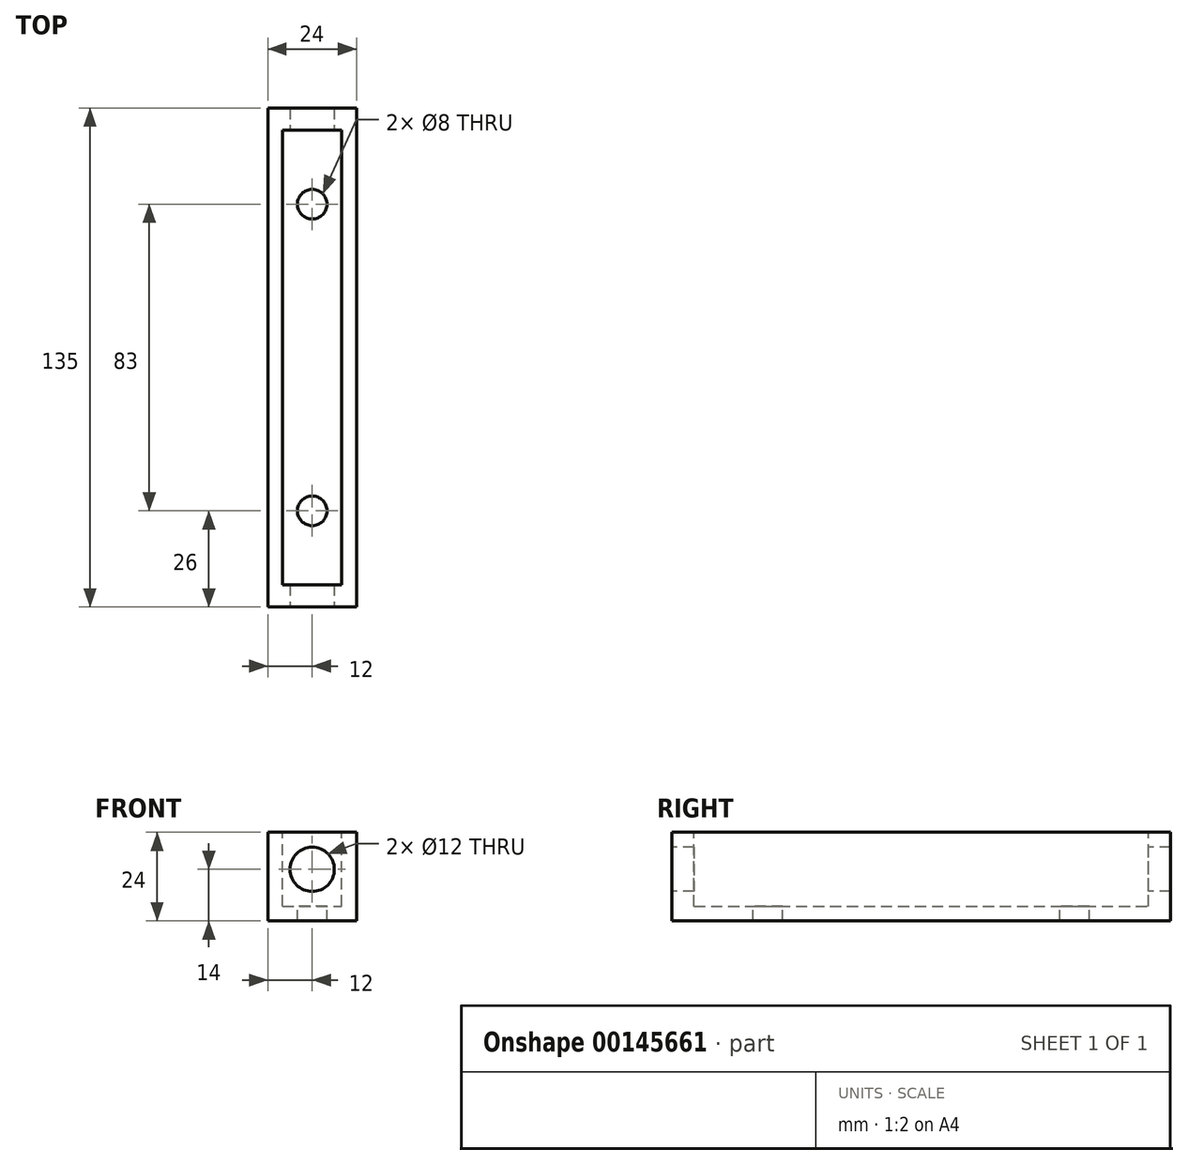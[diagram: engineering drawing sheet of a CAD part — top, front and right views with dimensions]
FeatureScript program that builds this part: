
annotation { "Feature Type Name" : "Feature", "Feature Type Description" : "" }
export const myFeature = defineFeature(function(context is Context, id is Id, definition is map)
    precondition{}
    {
        {
            var Q0;
            Q0=qCreatedBy(makeId("Front.planeOp"),FACE);
            var sketch = newSketch(context, id + "F0", { "sketchPlane" : qUnion([Q0])});
            skLineSegment(sketch, "E0", {"start": v(0, 0) * mm, "end": v(24, 0) * mm});
            skLineSegment(sketch, "E1", {"start": v(24, 0) * mm, "end": v(24, 24) * mm});
            skLineSegment(sketch, "E2", {"start": v(24, 24) * mm, "end": v(0, 24) * mm});
            skLineSegment(sketch, "E3", {"start": v(0, 24) * mm, "end": v(0, 0) * mm});
            skSolve(sketch);
        }
        {
            var Q0;
            Q0 = qSketchRegion(id + "F0", true);
            extrude(context, id + "F1", {"entities" : qUnion([Q0]), "depth" : 135 * mm});
        }
        {
            var Q0;
            Q0=makeQuery(id+"F1.opExtrude","SWEPT_FACE",FACE,{"disambiguationData":[OSD([sQuery(id+"F0.wireOp",EDGE,"E2")])]});
            var sketch = newSketch(context, id + "F2", { "sketchPlane" : qUnion([Q0])});
            skLineSegment(sketch, "E4", {"start": v(20, -129) * mm, "end": v(20, -6) * mm});
            skLineSegment(sketch, "E5", {"start": v(4, -129) * mm, "end": v(4, -6) * mm});
            skLineSegment(sketch, "E6", {"start": v(4, -6) * mm, "end": v(20, -6) * mm});
            skLineSegment(sketch, "E7", {"start": v(20, -129) * mm, "end": v(4, -129) * mm});
            skPoint(sketch, "E8.orphan", {"position": v(0, -129) * mm});
            skSolve(sketch);
        }
        {
            var Q0;
            Q0 = qSketchRegion(id + "F2", true);
            extrude(context, id + "F3", {"entities" : qUnion([Q0]), "operationType" : NewBodyOperationType.REMOVE, "oppositeDirection" : true, "depth" : 20 * mm});
        }
        {
            var Q0;
            Q0=makeQuery(id+"F1.opExtrude","CAP_FACE",FACE,{"disambiguationData":[OSD([sQuery(id+"F0.wireOp",EDGE,"E0"),sQuery(id+"F0.wireOp",EDGE,"E1"),sQuery(id+"F0.wireOp",EDGE,"E2"),sQuery(id+"F0.wireOp",EDGE,"E3")])],"isStart":false});
            var sketch = newSketch(context, id + "F4", { "sketchPlane" : qUnion([Q0])});
            skCircle(sketch, "E9", {"center": v(12, 14) * mm, "radius": 6 * mm});
            skSolve(sketch);
        }
        {
            var Q0;
            Q0 = qSketchRegion(id + "F4", true);
            extrude(context, id + "F5", {"entities" : qUnion([Q0]), "operationType" : NewBodyOperationType.REMOVE, "endBound" : BoundingType.THROUGH_ALL, "oppositeDirection" : true, "depth" : 25 * mm});
        }
        {
            var Q0;
            Q0=makeQuery(id+"F3.boolean.opBoolean","COPY",FACE,{"derivedFrom":makeQuery(id+"F3.opExtrude","CAP_FACE",FACE,{"disambiguationData":[OSD([sQuery(id+"F2.wireOp",EDGE,"E4"),sQuery(id+"F2.wireOp",EDGE,"E5"),sQuery(id+"F2.wireOp",EDGE,"E6"),sQuery(id+"F2.wireOp",EDGE,"E7")])],"isStart":false})});
            var sketch = newSketch(context, id + "F6", { "sketchPlane" : qUnion([Q0])});
            skCircle(sketch, "E10", {"center": v(12, -26) * mm, "radius": 4 * mm});
            skCircle(sketch, "E11", {"center": v(12, -109) * mm, "radius": 4 * mm});
            skSolve(sketch);
        }
        {
            var Q0;
            Q0 = qSketchRegion(id + "F6", true);
            extrude(context, id + "F7", {"entities" : qUnion([Q0]), "operationType" : NewBodyOperationType.REMOVE, "oppositeDirection" : true, "depth" : 25 * mm});
        }
    });
